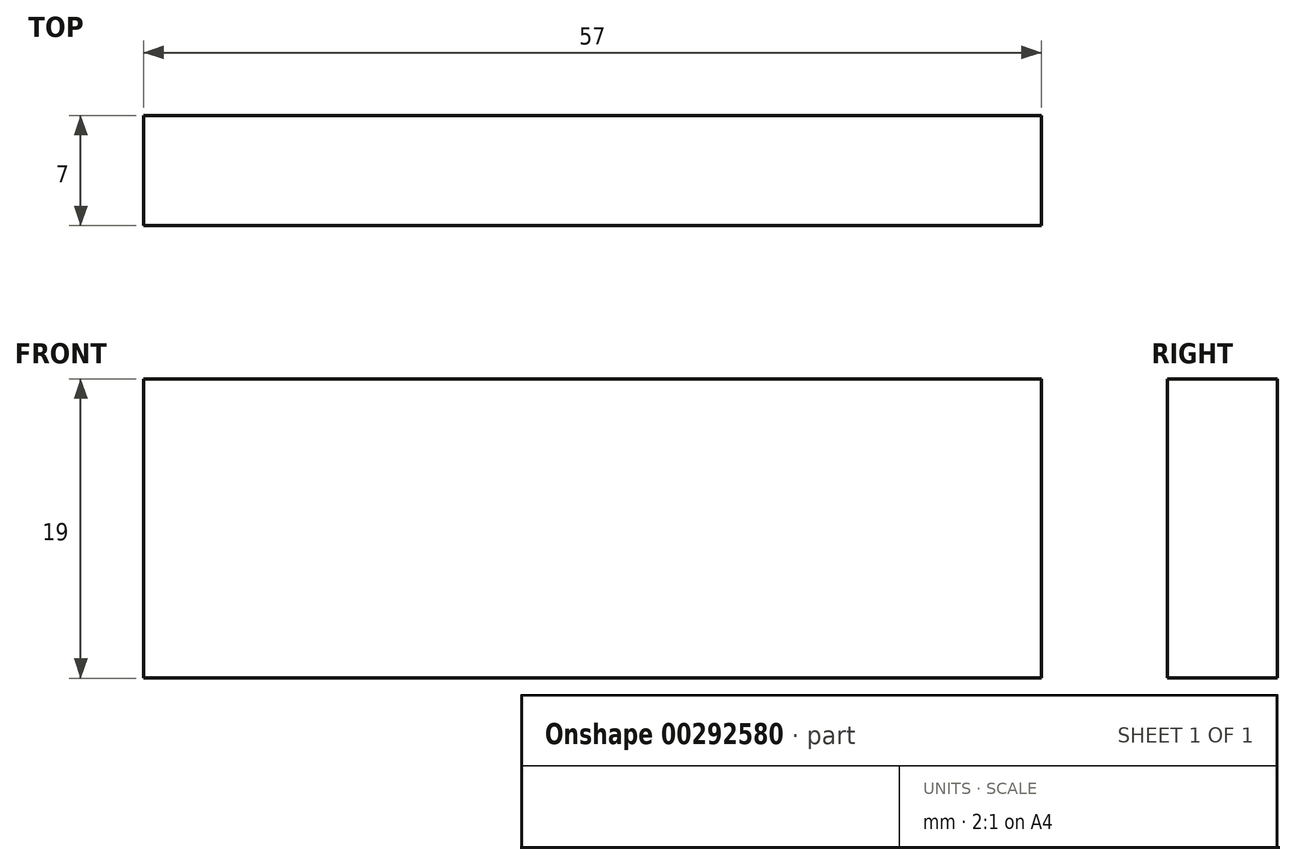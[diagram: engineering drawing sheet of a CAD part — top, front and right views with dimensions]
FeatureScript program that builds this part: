
annotation { "Feature Type Name" : "Feature", "Feature Type Description" : "" }
export const myFeature = defineFeature(function(context is Context, id is Id, definition is map)
    precondition{}
    {
        {
            var Q0;
            Q0=qCreatedBy(makeId("Front.planeOp"),FACE);
            var sketch = newSketch(context, id + "F0", { "sketchPlane" : qUnion([Q0])});
            skLineSegment(sketch, "E0", {"start": v(-22.64, 2.8) * mm, "end": v(34.36, 2.8) * mm});
            skLineSegment(sketch, "E1", {"start": v(34.36, 2.8) * mm, "end": v(34.36, -16.2) * mm});
            skLineSegment(sketch, "E2", {"start": v(34.36, -16.2) * mm, "end": v(-22.64, -16.2) * mm});
            skLineSegment(sketch, "E3", {"start": v(-22.64, -16.2) * mm, "end": v(-22.64, 2.8) * mm});
            skSolve(sketch);
        }
        {
            var Q0;
            Q0 = qSketchRegion(id + "F0", true);
            extrude(context, id + "F1", {"entities" : qUnion([Q0]), "depth" : 7 * mm});
        }
    });
